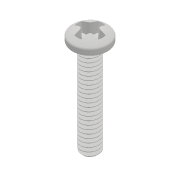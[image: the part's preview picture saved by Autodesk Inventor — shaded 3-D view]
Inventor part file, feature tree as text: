
AUTODESK INVENTOR PART (.ipt)
format: ipt  version: 2018 (Build 220112000, 112)  size: 1,042,432 bytes
history: native  units: mm
features: fillet x1
ambient origin geometry x8: Origin, YZ Plane, XZ Plane, XY Plane, X Axis, Y Axis, Z Axis, Center Point
bodies: Solid1 (feature_tree)
feature tree (1):
  fillet  "Fillet1"  [1 undecoded]
note: 1 required parameter value undecoded (feature->parameter linkage not recoverable at this tier; creation-order binding heuristic only, values carry confidence <= 0.55)
